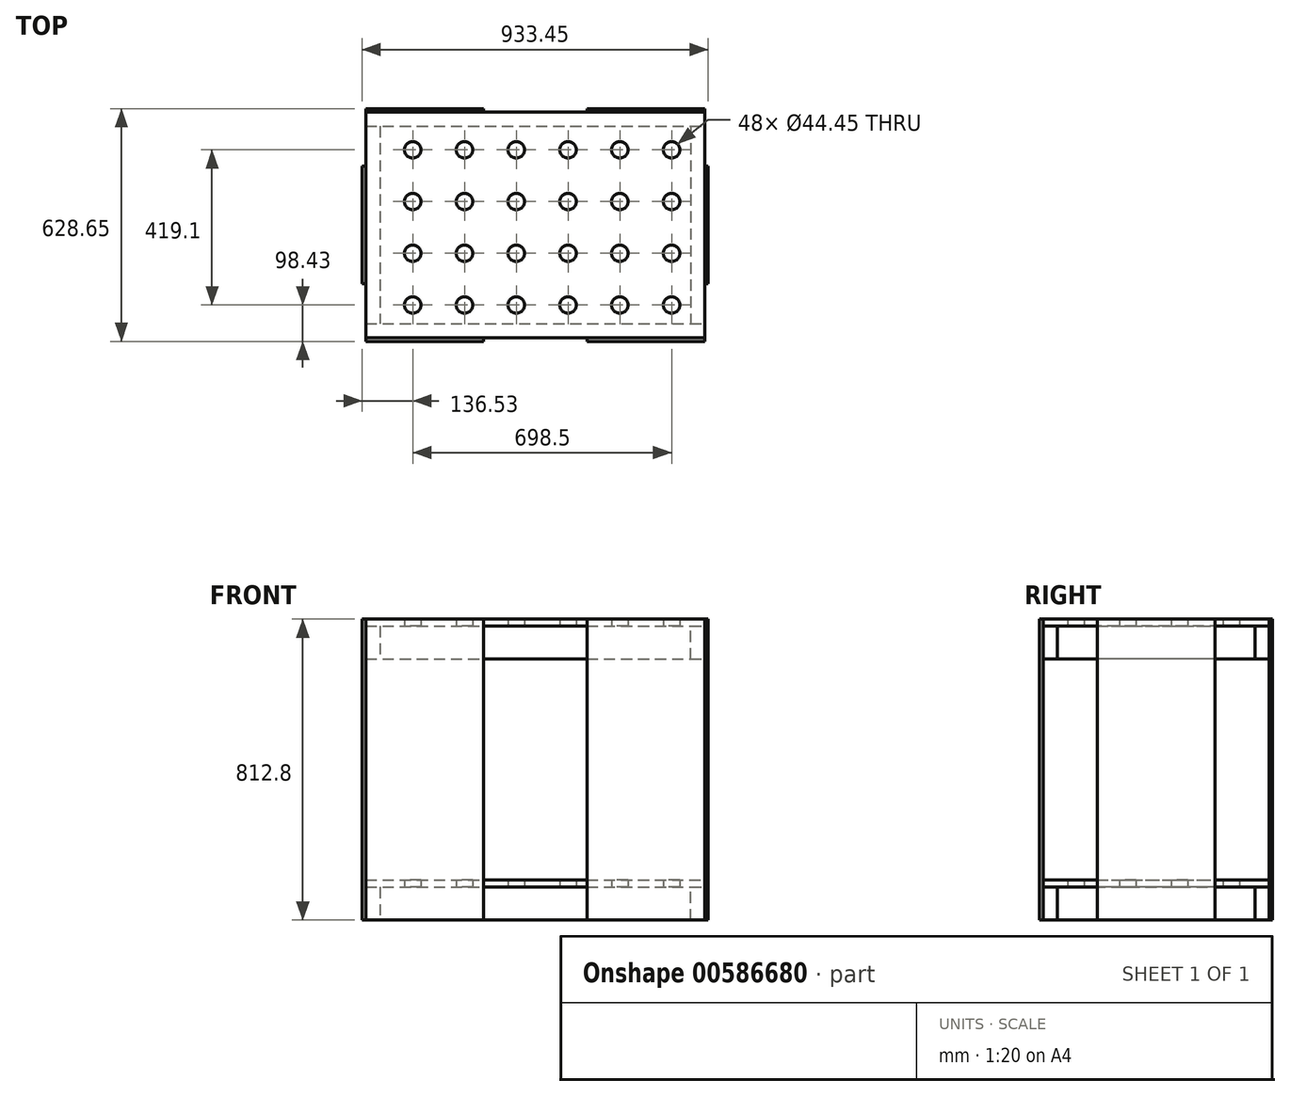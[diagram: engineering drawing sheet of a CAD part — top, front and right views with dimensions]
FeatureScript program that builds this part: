
annotation { "Feature Type Name" : "Feature", "Feature Type Description" : "" }
export const myFeature = defineFeature(function(context is Context, id is Id, definition is map)
    precondition{}
    {
        {
            var Q0;
            Q0=qCreatedBy(makeId("Front.planeOp"),FACE);
            var sketch = newSketch(context, id + "F0", { "sketchPlane" : qUnion([Q0])});
            skLineSegment(sketch, "E0.bottom", {"start": v(0, 0) * mm, "end": v(914.4, 0) * mm});
            skLineSegment(sketch, "E0.top", {"start": v(0, -88.9) * mm, "end": v(914.4, -88.9) * mm});
            skLineSegment(sketch, "E0.left", {"start": v(0, 0) * mm, "end": v(0, -88.9) * mm});
            skLineSegment(sketch, "E0.right", {"start": v(914.4, 0) * mm, "end": v(914.4, -88.9) * mm});
            skSolve(sketch);
        }
        {
            var Q0;
            Q0=makeQuery(id+"F0.imprint","IMPRINT",FACE,{"disambiguationData":[TD([[makeQuery(id+"F0.imprint","IMPRINT",EDGE,{"derivedFrom":sQuery(id+"F0.wireOp",EDGE,"E0.bottom")}),-1.0]])]});
            extrude(context, id + "F1", {"entities" : qUnion([Q0]), "depth" : 38.1 * mm, "offsetDistance" : 25.4 * mm});
        }
        {
            var Q0;
            Q0=makeQuery(id+"F1.opExtrude","CAP_FACE",FACE,{"disambiguationData":[OSD([sQuery(id+"F0.wireOp",EDGE,"E0.bottom"),sQuery(id+"F0.wireOp",EDGE,"E0.top"),sQuery(id+"F0.wireOp",EDGE,"E0.left"),sQuery(id+"F0.wireOp",EDGE,"E0.right")])],"isStart":true});
            var sketch = newSketch(context, id + "F2", { "sketchPlane" : qUnion([Q0])});
            skLineSegment(sketch, "E1.bottom", {"start": v(-914.4, -88.9) * mm, "end": v(-876.3, -88.9) * mm});
            skLineSegment(sketch, "E1.top", {"start": v(-914.4, 0) * mm, "end": v(-876.3, 0) * mm});
            skLineSegment(sketch, "E1.left", {"start": v(-914.4, -88.9) * mm, "end": v(-914.4, 0) * mm});
            skLineSegment(sketch, "E1.right", {"start": v(-876.3, -88.9) * mm, "end": v(-876.3, 0) * mm});
            skSolve(sketch);
        }
        {
            var Q0;
            Q0=makeQuery(id+"F2.imprint","IMPRINT",FACE,{"disambiguationData":[TD([[makeQuery(id+"F2.imprint","IMPRINT",EDGE,{"derivedFrom":sQuery(id+"F2.wireOp",EDGE,"E1.bottom")}),-1.0]])]});
            extrude(context, id + "F3", {"entities" : qUnion([Q0]), "depth" : 533.4 * mm, "offsetDistance" : 25.4 * mm});
        }
        {
            var Q0;
            Q0=makeQuery(id+"F3.opExtrude","SWEPT_BODY",BODY,{"disambiguationData":[OSD([sQuery(id+"F2.wireOp",EDGE,"E1.bottom"),sQuery(id+"F2.wireOp",EDGE,"E1.top"),sQuery(id+"F2.wireOp",EDGE,"E1.left"),sQuery(id+"F2.wireOp",EDGE,"E1.right")])]});
            transform(context, id + "F4", {"entities" : qUnion([Q0]), "transformType" : TransformType.TRANSLATION_3D, "dx" : -876.3 * mm, "dy" : 0 * mm, "dz" : 0 * mm, "makeCopy" : true});
        }
        {
            var Q0;
            Q0=makeQuery(id+"F1.opExtrude","SWEPT_BODY",BODY,{"disambiguationData":[OSD([sQuery(id+"F0.wireOp",EDGE,"E0.bottom"),sQuery(id+"F0.wireOp",EDGE,"E0.top"),sQuery(id+"F0.wireOp",EDGE,"E0.left"),sQuery(id+"F0.wireOp",EDGE,"E0.right")])]});
            transform(context, id + "F5", {"entities" : qUnion([Q0]), "transformType" : TransformType.TRANSLATION_3D, "dx" : 0 * mm, "dy" : 571.5 * mm, "dz" : 0 * mm, "makeCopy" : true});
        }
        {
            var Q0;
            Q0=qCreatedBy(makeId("Top.planeOp"),FACE);
            var sketch = newSketch(context, id + "F6", { "sketchPlane" : qUnion([Q0])});
            skLineSegment(sketch, "E2.bottom", {"start": v(0, -38.1) * mm, "end": v(914.4, -38.1) * mm});
            skLineSegment(sketch, "E2.top", {"start": v(0, 571.5) * mm, "end": v(914.4, 571.5) * mm});
            skLineSegment(sketch, "E2.left", {"start": v(0, -38.1) * mm, "end": v(0, 571.5) * mm});
            skLineSegment(sketch, "E2.right", {"start": v(914.4, -38.1) * mm, "end": v(914.4, 571.5) * mm});
            skSolve(sketch);
        }
        {
            var Q0;
            Q0=makeQuery(id+"F6.imprint","IMPRINT",FACE,{"disambiguationData":[TD([[makeQuery(id+"F6.imprint","IMPRINT",EDGE,{"derivedFrom":sQuery(id+"F6.wireOp",EDGE,"E2.bottom")}),1.0]])]});
            extrude(context, id + "F7", {"entities" : qUnion([Q0]), "depth" : 19.05 * mm, "offsetDistance" : 25.4 * mm});
        }
        {
            var Q0;
            Q0=qCreatedBy(makeId("Top.planeOp"),FACE);
            var sketch = newSketch(context, id + "F8", { "sketchPlane" : qUnion([Q0])});
            skCircle(sketch, "E3", {"center": v(825.5, 50.8) * mm, "radius": 22.23 * mm});
            skCircle(sketch, "E4.0.1.0", {"center": v(825.5, 190.5) * mm, "radius": 22.23 * mm});
            skCircle(sketch, "E4.0.2.0", {"center": v(825.5, 330.2) * mm, "radius": 22.23 * mm});
            skCircle(sketch, "E4.0.3.0", {"center": v(825.5, 469.9) * mm, "radius": 22.23 * mm});
            skCircle(sketch, "E4.1.0.0", {"center": v(685.8, 50.8) * mm, "radius": 22.23 * mm});
            skCircle(sketch, "E4.1.1.0", {"center": v(685.8, 190.5) * mm, "radius": 22.23 * mm});
            skCircle(sketch, "E4.1.2.0", {"center": v(685.8, 330.2) * mm, "radius": 22.23 * mm});
            skCircle(sketch, "E4.1.3.0", {"center": v(685.8, 469.9) * mm, "radius": 22.23 * mm});
            skCircle(sketch, "E4.2.0.0", {"center": v(546.1, 50.8) * mm, "radius": 22.23 * mm});
            skCircle(sketch, "E4.2.1.0", {"center": v(546.1, 190.5) * mm, "radius": 22.23 * mm});
            skCircle(sketch, "E4.2.2.0", {"center": v(546.1, 330.2) * mm, "radius": 22.23 * mm});
            skCircle(sketch, "E4.2.3.0", {"center": v(546.1, 469.9) * mm, "radius": 22.23 * mm});
            skCircle(sketch, "E4.3.0.0", {"center": v(406.4, 50.8) * mm, "radius": 22.23 * mm});
            skCircle(sketch, "E4.3.1.0", {"center": v(406.4, 190.5) * mm, "radius": 22.23 * mm});
            skCircle(sketch, "E4.3.2.0", {"center": v(406.4, 330.2) * mm, "radius": 22.23 * mm});
            skCircle(sketch, "E4.3.3.0", {"center": v(406.4, 469.9) * mm, "radius": 22.23 * mm});
            skCircle(sketch, "E4.4.0.0", {"center": v(266.7, 50.8) * mm, "radius": 22.23 * mm});
            skCircle(sketch, "E4.4.1.0", {"center": v(266.7, 190.5) * mm, "radius": 22.23 * mm});
            skCircle(sketch, "E4.4.2.0", {"center": v(266.7, 330.2) * mm, "radius": 22.23 * mm});
            skCircle(sketch, "E4.4.3.0", {"center": v(266.7, 469.9) * mm, "radius": 22.23 * mm});
            skCircle(sketch, "E4.5.0.0", {"center": v(127, 50.8) * mm, "radius": 22.23 * mm});
            skCircle(sketch, "E4.5.1.0", {"center": v(127, 190.5) * mm, "radius": 22.23 * mm});
            skCircle(sketch, "E4.5.2.0", {"center": v(127, 330.2) * mm, "radius": 22.23 * mm});
            skCircle(sketch, "E4.5.3.0", {"center": v(127, 469.9) * mm, "radius": 22.23 * mm});
            skLineSegment(sketch, "E4.direction1", {"start": v(825.5, 50.8) * mm, "end": v(685.8, 50.8) * mm, "construction": true});
            skLineSegment(sketch, "E4.direction2", {"start": v(825.5, 50.8) * mm, "end": v(825.5, 190.5) * mm, "construction": true});
            skSolve(sketch);
        }
        {
            var Q0;
            Q0=makeQuery(id+"F8.imprint","IMPRINT",FACE,{"disambiguationData":[TD([[makeQuery(id+"F8.imprint","IMPRINT",EDGE,{"derivedFrom":sQuery(id+"F8.wireOp",EDGE,"E4.4.2.0")}),1.0]])]});
            var Q1;
            Q1=makeQuery(id+"F8.imprint","IMPRINT",FACE,{"disambiguationData":[TD([[makeQuery(id+"F8.imprint","IMPRINT",EDGE,{"derivedFrom":sQuery(id+"F8.wireOp",EDGE,"E4.2.1.0")}),1.0]])]});
            var Q2;
            Q2=makeQuery(id+"F8.imprint","IMPRINT",FACE,{"disambiguationData":[TD([[makeQuery(id+"F8.imprint","IMPRINT",EDGE,{"derivedFrom":sQuery(id+"F8.wireOp",EDGE,"E4.5.1.0")}),1.0]])]});
            var Q3;
            Q3=makeQuery(id+"F8.imprint","IMPRINT",FACE,{"disambiguationData":[TD([[makeQuery(id+"F8.imprint","IMPRINT",EDGE,{"derivedFrom":sQuery(id+"F8.wireOp",EDGE,"E4.0.1.0")}),1.0]])]});
            var Q4;
            Q4=makeQuery(id+"F8.imprint","IMPRINT",FACE,{"disambiguationData":[TD([[makeQuery(id+"F8.imprint","IMPRINT",EDGE,{"derivedFrom":sQuery(id+"F8.wireOp",EDGE,"E3")}),1.0]])]});
            var Q5;
            Q5=makeQuery(id+"F8.imprint","IMPRINT",FACE,{"disambiguationData":[TD([[makeQuery(id+"F8.imprint","IMPRINT",EDGE,{"derivedFrom":sQuery(id+"F8.wireOp",EDGE,"E4.3.2.0")}),1.0]])]});
            var Q6;
            Q6=makeQuery(id+"F8.imprint","IMPRINT",FACE,{"disambiguationData":[TD([[makeQuery(id+"F8.imprint","IMPRINT",EDGE,{"derivedFrom":sQuery(id+"F8.wireOp",EDGE,"E4.3.1.0")}),1.0]])]});
            var Q7;
            Q7=makeQuery(id+"F8.imprint","IMPRINT",FACE,{"disambiguationData":[TD([[makeQuery(id+"F8.imprint","IMPRINT",EDGE,{"derivedFrom":sQuery(id+"F8.wireOp",EDGE,"E4.3.3.0")}),1.0]])]});
            var Q8;
            Q8=makeQuery(id+"F8.imprint","IMPRINT",FACE,{"disambiguationData":[TD([[makeQuery(id+"F8.imprint","IMPRINT",EDGE,{"derivedFrom":sQuery(id+"F8.wireOp",EDGE,"E4.5.0.0")}),1.0]])]});
            var Q9;
            Q9=makeQuery(id+"F8.imprint","IMPRINT",FACE,{"disambiguationData":[TD([[makeQuery(id+"F8.imprint","IMPRINT",EDGE,{"derivedFrom":sQuery(id+"F8.wireOp",EDGE,"E4.3.0.0")}),1.0]])]});
            var Q10;
            Q10=makeQuery(id+"F8.imprint","IMPRINT",FACE,{"disambiguationData":[TD([[makeQuery(id+"F8.imprint","IMPRINT",EDGE,{"derivedFrom":sQuery(id+"F8.wireOp",EDGE,"E4.2.2.0")}),1.0]])]});
            var Q11;
            Q11=makeQuery(id+"F8.imprint","IMPRINT",FACE,{"disambiguationData":[TD([[makeQuery(id+"F8.imprint","IMPRINT",EDGE,{"derivedFrom":sQuery(id+"F8.wireOp",EDGE,"E4.2.3.0")}),1.0]])]});
            var Q12;
            Q12=makeQuery(id+"F8.imprint","IMPRINT",FACE,{"disambiguationData":[TD([[makeQuery(id+"F8.imprint","IMPRINT",EDGE,{"derivedFrom":sQuery(id+"F8.wireOp",EDGE,"E4.4.0.0")}),1.0]])]});
            var Q13;
            Q13=makeQuery(id+"F8.imprint","IMPRINT",FACE,{"disambiguationData":[TD([[makeQuery(id+"F8.imprint","IMPRINT",EDGE,{"derivedFrom":sQuery(id+"F8.wireOp",EDGE,"E4.5.2.0")}),1.0]])]});
            var Q14;
            Q14=makeQuery(id+"F8.imprint","IMPRINT",FACE,{"disambiguationData":[TD([[makeQuery(id+"F8.imprint","IMPRINT",EDGE,{"derivedFrom":sQuery(id+"F8.wireOp",EDGE,"E4.2.0.0")}),1.0]])]});
            var Q15;
            Q15=makeQuery(id+"F8.imprint","IMPRINT",FACE,{"disambiguationData":[TD([[makeQuery(id+"F8.imprint","IMPRINT",EDGE,{"derivedFrom":sQuery(id+"F8.wireOp",EDGE,"E4.1.3.0")}),1.0]])]});
            var Q16;
            Q16=makeQuery(id+"F8.imprint","IMPRINT",FACE,{"disambiguationData":[TD([[makeQuery(id+"F8.imprint","IMPRINT",EDGE,{"derivedFrom":sQuery(id+"F8.wireOp",EDGE,"E4.0.3.0")}),1.0]])]});
            var Q17;
            Q17=makeQuery(id+"F8.imprint","IMPRINT",FACE,{"disambiguationData":[TD([[makeQuery(id+"F8.imprint","IMPRINT",EDGE,{"derivedFrom":sQuery(id+"F8.wireOp",EDGE,"E4.0.2.0")}),1.0]])]});
            var Q18;
            Q18=makeQuery(id+"F8.imprint","IMPRINT",FACE,{"disambiguationData":[TD([[makeQuery(id+"F8.imprint","IMPRINT",EDGE,{"derivedFrom":sQuery(id+"F8.wireOp",EDGE,"E4.4.1.0")}),1.0]])]});
            var Q19;
            Q19=makeQuery(id+"F8.imprint","IMPRINT",FACE,{"disambiguationData":[TD([[makeQuery(id+"F8.imprint","IMPRINT",EDGE,{"derivedFrom":sQuery(id+"F8.wireOp",EDGE,"E4.5.3.0")}),1.0]])]});
            var Q20;
            Q20=makeQuery(id+"F8.imprint","IMPRINT",FACE,{"disambiguationData":[TD([[makeQuery(id+"F8.imprint","IMPRINT",EDGE,{"derivedFrom":sQuery(id+"F8.wireOp",EDGE,"E4.1.2.0")}),1.0]])]});
            var Q21;
            Q21=makeQuery(id+"F8.imprint","IMPRINT",FACE,{"disambiguationData":[TD([[makeQuery(id+"F8.imprint","IMPRINT",EDGE,{"derivedFrom":sQuery(id+"F8.wireOp",EDGE,"E4.4.3.0")}),1.0]])]});
            var Q22;
            Q22=makeQuery(id+"F8.imprint","IMPRINT",FACE,{"disambiguationData":[TD([[makeQuery(id+"F8.imprint","IMPRINT",EDGE,{"derivedFrom":sQuery(id+"F8.wireOp",EDGE,"E4.1.1.0")}),1.0]])]});
            var Q23;
            Q23=makeQuery(id+"F8.imprint","IMPRINT",FACE,{"disambiguationData":[TD([[makeQuery(id+"F8.imprint","IMPRINT",EDGE,{"derivedFrom":sQuery(id+"F8.wireOp",EDGE,"E4.1.0.0")}),1.0]])]});
            extrude(context, id + "F9", {"entities" : qUnion([Q0, Q1, Q2, Q3, Q4, Q5, Q6, Q7, Q8, Q9, Q10, Q11, Q12, Q13, Q14, Q15, Q16, Q17, Q18, Q19, Q20, Q21, Q22, Q23]), "operationType" : NewBodyOperationType.REMOVE, "endBound" : BoundingType.UP_TO_NEXT, "depth" : 25.4 * mm, "offsetDistance" : 25.4 * mm});
        }
        {
            var Q0;
            Q0=qCreatedBy(makeId("Right.planeOp"),FACE);
            var sketch = newSketch(context, id + "F10", { "sketchPlane" : qUnion([Q0])});
            skLineSegment(sketch, "E5.bottom", {"start": v(279.4, -88.9) * mm, "end": v(-38.1, -88.9) * mm});
            skLineSegment(sketch, "E5.top", {"start": v(279.4, 723.9) * mm, "end": v(-38.1, 723.9) * mm});
            skLineSegment(sketch, "E5.left", {"start": v(279.4, -88.9) * mm, "end": v(279.4, 723.9) * mm});
            skLineSegment(sketch, "E5.right", {"start": v(-38.1, -88.9) * mm, "end": v(-38.1, 723.9) * mm});
            skSolve(sketch);
        }
        {
            var Q0;
            Q0=makeQuery(id+"F10.imprint","IMPRINT",FACE,{"disambiguationData":[TD([[makeQuery(id+"F10.imprint","IMPRINT",EDGE,{"derivedFrom":sQuery(id+"F10.wireOp",EDGE,"E5.bottom")}),-1.0]])]});
            extrude(context, id + "F11", {"entities" : qUnion([Q0]), "oppositeDirection" : true, "depth" : 9.52 * mm, "offsetDistance" : 25.4 * mm});
        }
        {
            var Q0;
            Q0=makeQuery(id+"F11.opExtrude","SWEPT_BODY",BODY,{"disambiguationData":[OSD([sQuery(id+"F10.wireOp",EDGE,"E5.bottom"),sQuery(id+"F10.wireOp",EDGE,"E5.top"),sQuery(id+"F10.wireOp",EDGE,"E5.left"),sQuery(id+"F10.wireOp",EDGE,"E5.right")])]});
            transform(context, id + "F12", {"entities" : qUnion([Q0]), "transformType" : TransformType.TRANSLATION_3D, "dx" : 923.92 * mm, "dy" : 0 * mm, "dz" : 0 * mm, "makeCopy" : true});
        }
        {
            var Q0;
            Q0=makeQuery(id+"F1.opExtrude","SWEPT_BODY",BODY,{"disambiguationData":[OSD([sQuery(id+"F0.wireOp",EDGE,"E0.bottom"),sQuery(id+"F0.wireOp",EDGE,"E0.top"),sQuery(id+"F0.wireOp",EDGE,"E0.left"),sQuery(id+"F0.wireOp",EDGE,"E0.right")])]});
            var Q1;
            Q1=makeQuery(id+"F3.opExtrude","SWEPT_BODY",BODY,{"disambiguationData":[OSD([sQuery(id+"F2.wireOp",EDGE,"E1.bottom"),sQuery(id+"F2.wireOp",EDGE,"E1.top"),sQuery(id+"F2.wireOp",EDGE,"E1.left"),sQuery(id+"F2.wireOp",EDGE,"E1.right")])]});
            var Q2;
            Q2=makeQuery(id+"F4.opPattern","COPY",BODY,{"derivedFrom":makeQuery(id+"F3.opExtrude","SWEPT_BODY",BODY,{"disambiguationData":[OSD([sQuery(id+"F2.wireOp",EDGE,"E1.bottom"),sQuery(id+"F2.wireOp",EDGE,"E1.top"),sQuery(id+"F2.wireOp",EDGE,"E1.left"),sQuery(id+"F2.wireOp",EDGE,"E1.right")])]}),"instanceName":"1"});
            var Q3;
            Q3=makeQuery(id+"F5.opPattern","COPY",BODY,{"derivedFrom":makeQuery(id+"F1.opExtrude","SWEPT_BODY",BODY,{"disambiguationData":[OSD([sQuery(id+"F0.wireOp",EDGE,"E0.bottom"),sQuery(id+"F0.wireOp",EDGE,"E0.top"),sQuery(id+"F0.wireOp",EDGE,"E0.left"),sQuery(id+"F0.wireOp",EDGE,"E0.right")])]}),"instanceName":"1"});
            var Q4;
            Q4=makeQuery(id+"F7.opExtrude","SWEPT_BODY",BODY,{"disambiguationData":[OSD([sQuery(id+"F6.wireOp",EDGE,"E2.bottom"),sQuery(id+"F6.wireOp",EDGE,"E2.top"),sQuery(id+"F6.wireOp",EDGE,"E2.left"),sQuery(id+"F6.wireOp",EDGE,"E2.right")])]});
            transform(context, id + "F13", {"entities" : qUnion([Q0, Q1, Q2, Q3, Q4]), "transformType" : TransformType.TRANSLATION_3D, "dx" : 0 * mm, "dy" : 0 * mm, "dz" : 704.85 * mm, "makeCopy" : true});
        }
        {
            var Q0;
            Q0=makeQuery(id+"F11.opExtrude","SWEPT_BODY",BODY,{"disambiguationData":[OSD([sQuery(id+"F10.wireOp",EDGE,"E5.bottom"),sQuery(id+"F10.wireOp",EDGE,"E5.top"),sQuery(id+"F10.wireOp",EDGE,"E5.left"),sQuery(id+"F10.wireOp",EDGE,"E5.right")])]});
            transform(context, id + "F14", {"entities" : qUnion([Q0]), "transformType" : TransformType.TRANSLATION_3D, "dx" : 0 * mm, "dy" : 609.6 * mm, "dz" : 0 * mm, "makeCopy" : true});
        }
        {
            var Q0;
            Q0=makeQuery(id+"F14.opPattern","COPY",BODY,{"derivedFrom":makeQuery(id+"F11.opExtrude","SWEPT_BODY",BODY,{"disambiguationData":[OSD([sQuery(id+"F10.wireOp",EDGE,"E5.bottom"),sQuery(id+"F10.wireOp",EDGE,"E5.top"),sQuery(id+"F10.wireOp",EDGE,"E5.left"),sQuery(id+"F10.wireOp",EDGE,"E5.right")])]}),"instanceName":"1"});
            var Q1;
            Q1=makeQuery(id+"F14.opPattern","COPY",EDGE,{"derivedFrom":makeQuery(id+"F11.opExtrude","CAP_EDGE",EDGE,{"disambiguationData":[OSD([sQuery(id+"F10.wireOp",EDGE,"E5.right")])],"isStart":true}),"instanceName":"1"});
            transform(context, id + "F15", {"entities" : qUnion([Q0]), "transformType" : TransformType.ROTATION, "transformAxis" : qUnion([Q1]), "angle" : 90 * degree, "oppositeDirection" : true, "makeCopy" : false});
        }
        {
            var Q0;
            Q0=makeQuery(id+"F14.opPattern","COPY",BODY,{"derivedFrom":makeQuery(id+"F11.opExtrude","SWEPT_BODY",BODY,{"disambiguationData":[OSD([sQuery(id+"F10.wireOp",EDGE,"E5.bottom"),sQuery(id+"F10.wireOp",EDGE,"E5.top"),sQuery(id+"F10.wireOp",EDGE,"E5.left"),sQuery(id+"F10.wireOp",EDGE,"E5.right")])]}),"instanceName":"1"});
            var Q1;
            Q1=makeQuery(id+"F14.opPattern","COPY",VERTEX,{"derivedFrom":makeQuery(id+"F11.opExtrude","CAP_VERTEX",VERTEX,{"disambiguationData":[OSD([sQuery(id+"F10.wireOp",EDGE,"E5.top"),sQuery(id+"F10.wireOp",EDGE,"E5.left")])],"isStart":true}),"instanceName":"1"});
            var Q2;
            Q2=makeQuery(id+"F13.opPattern","COPY",VERTEX,{"derivedFrom":makeQuery(id+"F7.opExtrude","CAP_VERTEX",VERTEX,{"disambiguationData":[OSD([sQuery(id+"F6.wireOp",EDGE,"E2.top"),sQuery(id+"F6.wireOp",EDGE,"E2.right")])],"isStart":false}),"instanceName":"1"});
            transform(context, id + "F16", {"entities" : qUnion([Q0]), "transformType" : TransformType.TRANSLATION_ENTITY, "oppositeDirectionEntity" : false, "transformLine" : qUnion([Q1, Q2]), "makeCopy" : true});
        }
        {
            var Q0;
            Q0=makeQuery(id+"F16.opPattern","COPY",BODY,{"derivedFrom":makeQuery(id+"F14.opPattern","COPY",BODY,{"derivedFrom":makeQuery(id+"F11.opExtrude","SWEPT_BODY",BODY,{"disambiguationData":[OSD([sQuery(id+"F10.wireOp",EDGE,"E5.bottom"),sQuery(id+"F10.wireOp",EDGE,"E5.top"),sQuery(id+"F10.wireOp",EDGE,"E5.left"),sQuery(id+"F10.wireOp",EDGE,"E5.right")])]}),"instanceName":"1"}),"instanceName":"1"});
            var Q1;
            Q1=makeQuery(id+"F16.opPattern","COPY",VERTEX,{"derivedFrom":makeQuery(id+"F14.opPattern","COPY",VERTEX,{"derivedFrom":makeQuery(id+"F11.opExtrude","CAP_VERTEX",VERTEX,{"disambiguationData":[OSD([sQuery(id+"F10.wireOp",EDGE,"E5.top"),sQuery(id+"F10.wireOp",EDGE,"E5.left")])],"isStart":false}),"instanceName":"1"}),"instanceName":"1"});
            var Q2;
            Q2=makeQuery(id+"F13.opPattern","COPY",VERTEX,{"derivedFrom":makeQuery(id+"F7.opExtrude","CAP_VERTEX",VERTEX,{"disambiguationData":[OSD([sQuery(id+"F6.wireOp",EDGE,"E2.bottom"),sQuery(id+"F6.wireOp",EDGE,"E2.right")])],"isStart":false}),"instanceName":"1"});
            transform(context, id + "F17", {"entities" : qUnion([Q0]), "transformType" : TransformType.TRANSLATION_ENTITY, "oppositeDirectionEntity" : false, "transformLine" : qUnion([Q1, Q2]), "makeCopy" : true});
        }
        {
            var Q0;
            Q0=makeQuery(id+"F14.opPattern","COPY",BODY,{"derivedFrom":makeQuery(id+"F11.opExtrude","SWEPT_BODY",BODY,{"disambiguationData":[OSD([sQuery(id+"F10.wireOp",EDGE,"E5.bottom"),sQuery(id+"F10.wireOp",EDGE,"E5.top"),sQuery(id+"F10.wireOp",EDGE,"E5.left"),sQuery(id+"F10.wireOp",EDGE,"E5.right")])]}),"instanceName":"1"});
            var Q1;
            Q1=makeQuery(id+"F14.opPattern","COPY",VERTEX,{"derivedFrom":makeQuery(id+"F11.opExtrude","CAP_VERTEX",VERTEX,{"disambiguationData":[OSD([sQuery(id+"F10.wireOp",EDGE,"E5.top"),sQuery(id+"F10.wireOp",EDGE,"E5.right")])],"isStart":false}),"instanceName":"1"});
            var Q2;
            Q2=makeQuery(id+"F13.opPattern","COPY",VERTEX,{"derivedFrom":makeQuery(id+"F7.opExtrude","CAP_VERTEX",VERTEX,{"disambiguationData":[OSD([sQuery(id+"F6.wireOp",EDGE,"E2.bottom"),sQuery(id+"F6.wireOp",EDGE,"E2.left")])],"isStart":false}),"instanceName":"1"});
            transform(context, id + "F18", {"entities" : qUnion([Q0]), "transformType" : TransformType.TRANSLATION_ENTITY, "oppositeDirectionEntity" : false, "transformLine" : qUnion([Q1, Q2]), "makeCopy" : true});
        }
        {
            var Q0;
            Q0=makeQuery(id+"F11.opExtrude","SWEPT_BODY",BODY,{"disambiguationData":[OSD([sQuery(id+"F10.wireOp",EDGE,"E5.bottom"),sQuery(id+"F10.wireOp",EDGE,"E5.top"),sQuery(id+"F10.wireOp",EDGE,"E5.left"),sQuery(id+"F10.wireOp",EDGE,"E5.right")])]});
            transform(context, id + "F19", {"entities" : qUnion([Q0]), "transformType" : TransformType.TRANSLATION_3D, "dx" : 0 * mm, "dy" : 146.05 * mm, "dz" : 0 * mm, "makeCopy" : false});
        }
        {
            var Q0;
            Q0=makeQuery(id+"F12.opPattern","COPY",BODY,{"derivedFrom":makeQuery(id+"F11.opExtrude","SWEPT_BODY",BODY,{"disambiguationData":[OSD([sQuery(id+"F10.wireOp",EDGE,"E5.bottom"),sQuery(id+"F10.wireOp",EDGE,"E5.top"),sQuery(id+"F10.wireOp",EDGE,"E5.left"),sQuery(id+"F10.wireOp",EDGE,"E5.right")])]}),"instanceName":"1"});
            transform(context, id + "F20", {"entities" : qUnion([Q0]), "transformType" : TransformType.TRANSLATION_3D, "dx" : 0 * mm, "dy" : 146.05 * mm, "dz" : 0 * mm, "makeCopy" : false});
        }
    });
